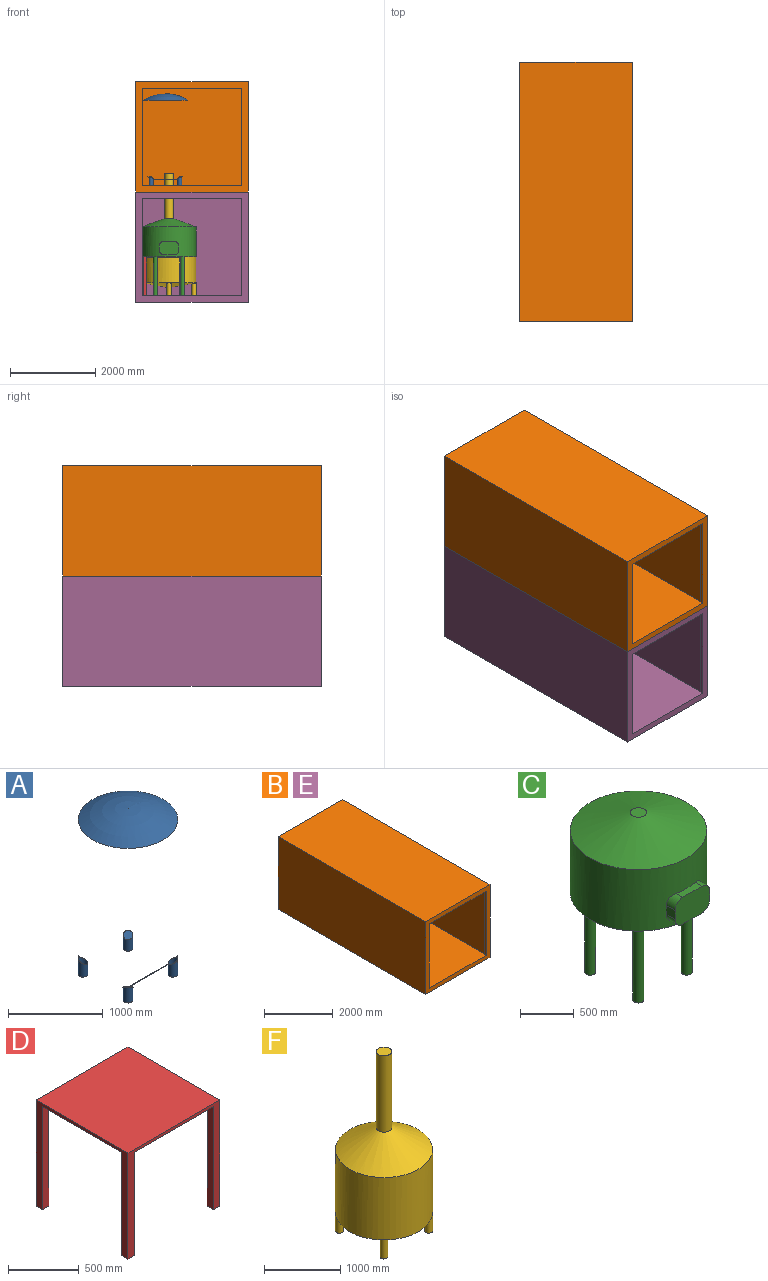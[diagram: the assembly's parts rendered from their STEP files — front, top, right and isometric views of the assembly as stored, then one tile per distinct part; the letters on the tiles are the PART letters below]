
ASSEMBLY  parts=6 mates=7
PART A: 11 faces, bbox 1050x1050x2150 mm
  f0: cylinder r=525mm len=1800mm, axis (0,0,-1), area 5937610.1mm2, adj f1,f2
  f1: sphere r=993.75mm, area 936587.3mm2, adj f0
  f2: sphere r=993.75mm, area -954968.1mm2, adj f0,f3,f4,f5,f6
  f3: cylinder r=50.8mm len=200mm, axis (0,0,1), area 54944.8mm2, adj f2,f7
  f4: cylinder r=50.8mm len=200mm, axis (0,0,1), area 54943.1mm2, adj f2,f8
  f5: cylinder r=50.8mm len=200mm, axis (0,0,1), area 54941.3mm2, adj f2,f9
  f6: cylinder r=50.8mm len=200mm, axis (0,0,1), area 54943mm2, adj f2,f10
  f7: plane 101.6x101.6mm, normal (0,0,1), area 8107.3mm2, adj f3
  f8: plane 101.6x101.6mm, normal (0,0,1), area 8107.3mm2, adj f4
  f9: plane 101.6x101.6mm, normal (0,0,-1), area 8107.3mm2, adj f5
  f10: plane 101.6x101.6mm, normal (0,0,1), area 8107.3mm2, adj f6
PART B: 15 faces, bbox 2641.6x6057.9x2583.2 mm
  f0: plane 2380x2349.5mm, normal (0,1,0), area 279410mm2, adj f1,f2,f3,f5,f6,f7,f8
  f1: plane 5892.8x2349.5mm, normal (0,0,-1), area 13845133.6mm2, adj f0,f2,f3,f4
  f2: plane 5892.8x2380mm, normal (-1,0,0), area 14024864mm2, adj f0,f1,f4,f5
  f3: plane 5892.8x2380mm, normal (1,0,0), area 14024864mm2, adj f0,f1,f4,f5
  f4: plane 2380x2349.5mm, normal (0,-1,0), area 5591810mm2, adj f1,f2,f3,f5
  f5: plane 5975.35x2349.5mm, normal (0,0,1), area 14037475.1mm2, adj f0,f2,f3,f4,f7,f8,f12
  f6: plane 2330x82.55mm, normal (0,0,-1), area 192341.5mm2, adj f0,f7,f8,f12
  f7: plane 2280x82.55mm, normal (-1,0,0), area 188214mm2, adj f0,f5,f6,f12
  f8: plane 2280x82.55mm, normal (1,0,0), area 188214mm2, adj f0,f5,f6,f12
  f9: plane 6057.9x2583.2mm, normal (1,0,0), area 15648767.3mm2, adj f10,f12,f13,f14
  f10: plane 2641.6x2583.2mm, normal (0,1,0), area 6823781.1mm2, adj f9,f11,f13,f14
  f11: plane 6057.9x2583.2mm, normal (-1,0,0), area 15648767.3mm2, adj f10,f12,f13,f14
  f12: plane 2641.6x2583.2mm, normal (0,-1,0), area 1511381.1mm2, adj f5,f6,f7,f8,f9,f11,f13,f14
  f13: plane 6057.9x2641.6mm, normal (0,0,1), area 16002548.6mm2, adj f9,f10,f11,f12
  f14: plane 6057.9x2641.6mm, normal (0,0,-1), area 16002548.6mm2, adj f9,f10,f11,f12
PART C: 21 faces, bbox 1270x1346.2x1817.6 mm
  f0: cylinder r=635mm len=1270mm, axis (0,0,-1), area 2659695.2mm2, adj f1,f11,f12,f13,f14,f15,f16,f18
  f1: plane 1270x1270mm, normal (0,0,-1), area 1234339.4mm2, adj f0,f2,f4,f6,f8
  f2: cylinder r=50.8mm len=914.4mm, axis (0,0,1), area 291863.5mm2, adj f1,f3
  f3: plane 101.6x101.6mm, normal (0,0,-1), area 8107.3mm2, adj f2
  f4: cylinder r=50.8mm len=914.4mm, axis (0,0,1), area 291863.5mm2, adj f1,f5
  f5: plane 101.6x101.6mm, normal (0,0,-1), area 8107.3mm2, adj f4
  f6: cylinder r=50.8mm len=914.4mm, axis (0,0,1), area 291863.5mm2, adj f1,f7
  f7: plane 101.6x101.6mm, normal (0,0,-1), area 8107.3mm2, adj f6
  f8: cylinder r=50.8mm len=914.4mm, axis (0,0,1), area 291863.5mm2, adj f1,f9
  f9: plane 101.6x101.6mm, normal (0,0,-1), area 8107.3mm2, adj f8
  f10: plane 152.4x152.4mm, normal (0,0,1), area 18241.5mm2, adj f11
  f11: cone r=76.2mm half-angle=70deg, axis (0,0,-1), area 1328512.4mm2, adj f0,f10
  f12: cylinder r=101.6mm len=118.78mm, axis (0,1,0), area 17029.3mm2, adj f0,f13,f17,f18
  f13: plane 254x89.03mm, normal (0,0,1), area 20436.6mm2, adj f0,f12,f14,f17
  f14: cylinder r=101.6mm len=118.78mm, axis (0,1,0), area 17029.2mm2, adj f0,f13,f15,f17
  f15: plane 118.78x101.6mm, normal (-1,0,0), area 12067.6mm2, adj f0,f14,f16,f17
  f16: cylinder r=101.6mm len=118.78mm, axis (0,1,0), area 17029.3mm2, adj f0,f15,f17,f19
  f17: plane 457.2x304.8mm, normal (0,-1,0), area 130493.6mm2, adj f12,f13,f14,f15,f16,f18,f19,f20
  f18: plane 118.78x101.6mm, normal (1,0,0), area 12067.6mm2, adj f0,f12,f17,f20
  f19: plane 254x89.03mm, normal (0,0,-1), area 20436.6mm2, adj f0,f16,f17,f20
  f20: cylinder r=101.6mm len=118.78mm, axis (0,1,0), area 17029.2mm2, adj f0,f17,f18,f19
PART D: 18 faces, bbox 914.4x914.4x914.4 mm
  f0: plane 914.4x914.4mm, normal (1,0,0), area 136128.8mm2, adj f1,f3,f4,f5,f9,f11,f15,f17
  f1: plane 914.4x914.4mm, normal (0,1,0), area 136128.8mm2, adj f0,f2,f4,f5,f13,f14,f16,f17
  f2: plane 914.4x914.4mm, normal (-1,0,0), area 136128.8mm2, adj f1,f3,f4,f5,f6,f8,f12,f14
  f3: plane 914.4x914.4mm, normal (0,-1,0), area 136128.8mm2, adj f0,f2,f4,f5,f7,f8,f10,f11
  f4: plane 914.4x914.4mm, normal (0,0,1), area 836127.4mm2, adj f0,f1,f2,f3
  f5: plane 914.4x914.4mm, normal (0,0,-1), area 819998.4mm2, adj f0,f1,f2,f3,f6,f7,f9,f10
  f6: plane 889x63.5mm, normal (0,1,0), area 56451.5mm2, adj f2,f5,f7,f8
  f7: plane 889x63.5mm, normal (1,0,0), area 56451.5mm2, adj f3,f5,f6,f8
  f8: plane 63.5x63.5mm, normal (0,0,-1), area 4032.2mm2, adj f2,f3,f6,f7
  f9: plane 889x63.5mm, normal (0,1,0), area 56451.5mm2, adj f0,f5,f10,f11
  f10: plane 889x63.5mm, normal (-1,0,0), area 56451.5mm2, adj f3,f5,f9,f11
  f11: plane 63.5x63.5mm, normal (0,0,-1), area 4032.3mm2, adj f0,f3,f9,f10
  f12: plane 889x63.5mm, normal (0,-1,0), area 56451.5mm2, adj f2,f5,f13,f14
  f13: plane 889x63.5mm, normal (1,0,0), area 56451.5mm2, adj f1,f5,f12,f14
  f14: plane 63.5x63.5mm, normal (0,0,-1), area 4032.2mm2, adj f1,f2,f12,f13
  f15: plane 889x63.5mm, normal (0,-1,0), area 56451.5mm2, adj f0,f5,f16,f17
  f16: plane 889x63.5mm, normal (-1,0,0), area 56451.5mm2, adj f1,f5,f15,f17
  f17: plane 63.5x63.5mm, normal (0,0,-1), area 4032.2mm2, adj f0,f1,f15,f16
PART E: same geometry as B
PART F: 18 faces, bbox 1270x1270x2874 mm
  f0: cylinder r=635mm len=1270mm, axis (0,0,-1), area 3989822.7mm2, adj f1,f2
  f1: cone r=101.6mm half-angle=56.7deg, axis (0,0,-1), area 1476342.4mm2, adj f0,f3
  f2: cone r=19.05mm half-angle=80deg, axis (0,0,1), area 1285153mm2, adj f0,f4
  f3: cylinder r=101.6mm len=1219.2mm, axis (0,0,-1), area 778302.7mm2, adj f1,f5
  f4: plane 38.1x38.1mm, normal (0,0,-1), area 1140.1mm2, adj f2
  f5: plane 203.2x203.2mm, normal (0,0,1), area 32429.3mm2, adj f3
  f6: cone r=19.05mm half-angle=80deg, axis (0,0,1), area 8231.4mm2, adj f7
  f7: cylinder r=50.8mm len=304.8mm, axis (0,0,1), area 94491.6mm2, adj f6,f8
  f8: plane 101.6x101.6mm, normal (0,0,-1), area 8107.3mm2, adj f7
  f9: cone r=19.05mm half-angle=80deg, axis (0,0,1), area 8234.8mm2, adj f10
  f10: cylinder r=50.8mm len=304.8mm, axis (0,0,1), area 94491.8mm2, adj f9,f11
  f11: plane 101.6x101.6mm, normal (0,0,-1), area 8107.3mm2, adj f10
  f12: cone r=19.05mm half-angle=80deg, axis (0,0,1), area 8230.1mm2, adj f13
  f13: cylinder r=50.8mm len=304.8mm, axis (0,0,1), area 94489.8mm2, adj f12,f14
  f14: plane 101.6x101.6mm, normal (0,0,-1), area 8107.3mm2, adj f13
  f15: cone r=19.05mm half-angle=80deg, axis (0,0,1), area 8231.5mm2, adj f16
  f16: cylinder r=50.8mm len=304.8mm, axis (0,0,1), area 94491mm2, adj f15,f17
  f17: plane 101.6x101.6mm, normal (0,0,-1), area 8107.3mm2, adj f16
PLACE A t=(-7790.78,1693.91,3467.98)mm
PLACE B t=(-1967.32,80.16,3267.98)mm
PLACE C rot(axis=(0,0,1),0.4deg) t=(-4583.02,54.43,1599.18)mm
PLACE D t=(-6401.65,-2391.96,1573.78)mm
PLACE E t=(-1967.32,80.16,684.78)mm fixed
PLACE F rot(axis=(0,0,1),45deg) t=(-5301.06,-437.87,989.58)mm
MATE planar B.f10 <-> E.f10  axis (0,1,0) through (-1967.32,3109.11,4407.18)mm
MATE planar A.f5 <-> B.f5  axis (0,0,-1) through (-2257.32,2029.22,3267.98)mm
MATE planar E.f5 <-> F.f16  axis (0,0,1) through (-1967.32,39.22,684.78)mm
MATE planar E.f5 <-> C.f8  axis (0,0,1) through (-1967.32,39.22,684.78)mm
MATE planar B.f9 <-> E.f9  axis (1,0,0) through (-646.52,80.16,4407.18)mm
MATE planar B.f14 <-> E.f13  axis (0,0,-1) through (-1967.32,80.16,3115.58)mm
MATE planar E.f5 <-> D.f17  axis (0,0,1) through (-1967.32,39.22,684.78)mm
